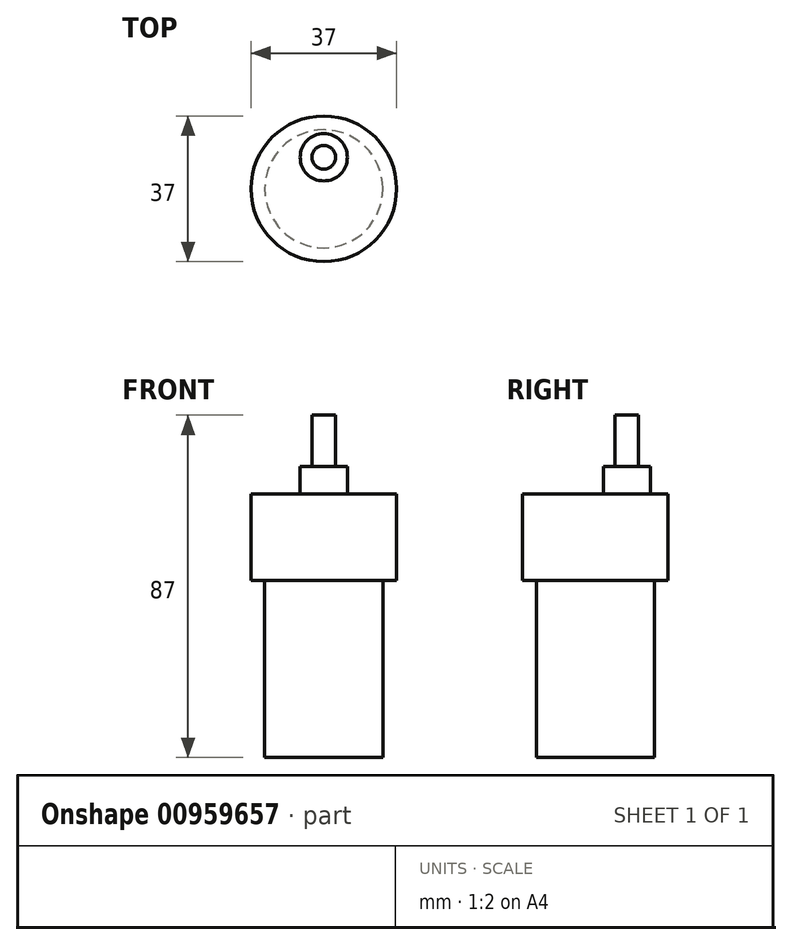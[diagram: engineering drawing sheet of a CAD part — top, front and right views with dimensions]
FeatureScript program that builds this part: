
annotation { "Feature Type Name" : "Feature", "Feature Type Description" : "" }
export const myFeature = defineFeature(function(context is Context, id is Id, definition is map)
    precondition{}
    {
        {
            var Q0;
            Q0=qCreatedBy(makeId("Top.planeOp"),FACE);
            var sketch = newSketch(context, id + "F0", { "sketchPlane" : qUnion([Q0])});
            skCircle(sketch, "E0", {"center": v(0, 0) * mm, "radius": 18.5 * mm});
            skSolve(sketch);
        }
        {
            var Q0;
            Q0=makeQuery(id+"F0.imprint","IMPRINT",FACE,{"disambiguationData":[TD([[makeQuery(id+"F0.imprint","IMPRINT",EDGE,{"derivedFrom":sQuery(id+"F0.wireOp",EDGE,"E0")}),1.0]])]});
            extrude(context, id + "F1", {"entities" : qUnion([Q0]), "depth" : 22 * mm, "offsetDistance" : 25 * mm});
        }
        {
            var Q0;
            Q0=makeQuery(id+"F1.opExtrude","CAP_FACE",FACE,{"disambiguationData":[OSD([sQuery(id+"F0.wireOp",EDGE,"E0")])],"isStart":true});
            var sketch = newSketch(context, id + "F2", { "sketchPlane" : qUnion([Q0])});
            skCircle(sketch, "E1", {"center": v(0, 0) * mm, "radius": 15 * mm});
            skSolve(sketch);
        }
        {
            var Q0;
            Q0=makeQuery(id+"F2.imprint","IMPRINT",FACE,{"disambiguationData":[TD([[makeQuery(id+"F2.imprint","IMPRINT",EDGE,{"derivedFrom":sQuery(id+"F2.wireOp",EDGE,"E1")}),1.0]])]});
            extrude(context, id + "F3", {"entities" : qUnion([Q0]), "operationType" : NewBodyOperationType.ADD, "depth" : 45 * mm, "offsetDistance" : 25 * mm});
        }
        {
            var Q0;
            Q0=makeQuery(id+"F1.opExtrude","CAP_FACE",FACE,{"disambiguationData":[OSD([sQuery(id+"F0.wireOp",EDGE,"E0")])],"isStart":false});
            var sketch = newSketch(context, id + "F4", { "sketchPlane" : qUnion([Q0])});
            skCircle(sketch, "E2", {"center": v(0, 8) * mm, "radius": 6 * mm});
            skSolve(sketch);
        }
        {
            var Q0;
            Q0=makeQuery(id+"F4.imprint","IMPRINT",FACE,{"disambiguationData":[TD([[makeQuery(id+"F4.imprint","IMPRINT",EDGE,{"derivedFrom":sQuery(id+"F4.wireOp",EDGE,"E2")}),1.0]])]});
            extrude(context, id + "F5", {"entities" : qUnion([Q0]), "operationType" : NewBodyOperationType.ADD, "depth" : 7 * mm, "offsetDistance" : 25 * mm});
        }
        {
            var Q0;
            Q0=makeQuery(id+"F5.opExtrude","CAP_FACE",FACE,{"disambiguationData":[OSD([sQuery(id+"F4.wireOp",EDGE,"E2")])],"isStart":false});
            var sketch = newSketch(context, id + "F6", { "sketchPlane" : qUnion([Q0])});
            skCircle(sketch, "E3", {"center": v(0, 8) * mm, "radius": 3 * mm});
            skSolve(sketch);
        }
        {
            var Q0;
            Q0=makeQuery(id+"F6.imprint","IMPRINT",FACE,{"disambiguationData":[TD([[makeQuery(id+"F6.imprint","IMPRINT",EDGE,{"derivedFrom":sQuery(id+"F6.wireOp",EDGE,"E3")}),1.0]])]});
            extrude(context, id + "F7", {"entities" : qUnion([Q0]), "operationType" : NewBodyOperationType.ADD, "depth" : 13 * mm, "offsetDistance" : 25 * mm});
        }
    });
